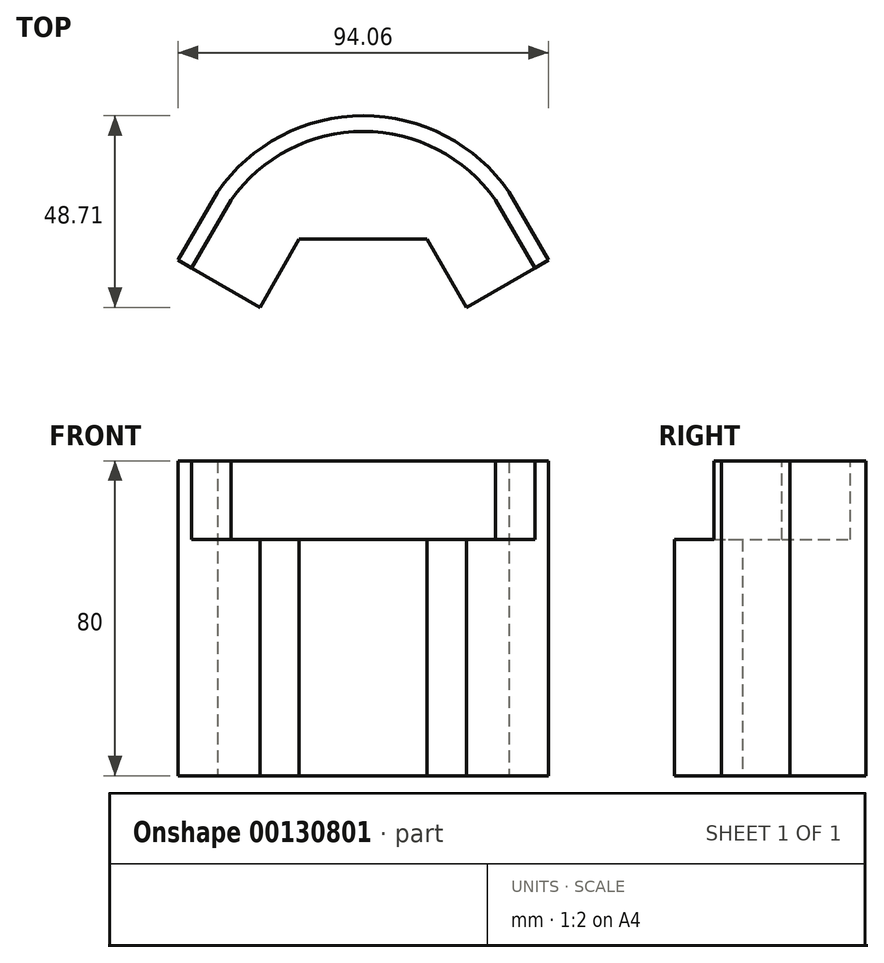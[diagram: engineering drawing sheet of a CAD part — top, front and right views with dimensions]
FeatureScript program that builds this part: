
annotation { "Feature Type Name" : "Feature", "Feature Type Description" : "" }
export const myFeature = defineFeature(function(context is Context, id is Id, definition is map)
    precondition{}
    {
        {
            var Q0;
            Q0=qCreatedBy(makeId("Top.planeOp"),FACE);
            var sketch = newSketch(context, id + "F0", { "sketchPlane" : qUnion([Q0])});
            skLineSegment(sketch, "E0", {"start": v(0, 0) * mm, "end": v(-43.57, -75.47) * mm});
            skLineSegment(sketch, "E1", {"start": v(0, -40) * mm, "end": v(-26.25, -85.47) * mm});
            skLineSegment(sketch, "E2", {"start": v(0, -40) * mm, "end": v(26.25, -85.47) * mm});
            skLineSegment(sketch, "E3", {"start": v(0, 0) * mm, "end": v(43.57, -75.47) * mm});
            skLineSegment(sketch, "E4", {"start": v(26.25, -85.47) * mm, "end": v(43.57, -75.47) * mm});
            skLineSegment(sketch, "E5", {"start": v(-26.25, -85.47) * mm, "end": v(-43.57, -75.47) * mm});
            skLineSegment(sketch, "E6", {"start": v(-33.57, -58.15) * mm, "end": v(-16.25, -68.15) * mm});
            skLineSegment(sketch, "E7", {"start": v(33.57, -58.15) * mm, "end": v(16.25, -68.15) * mm});
            skCircle(sketch, "E8", {"center": v(0, -77.53) * mm, "radius": 38.76 * mm});
            skSolve(sketch);
        }
        {
            var Q0;
            Q0=qCreatedBy(makeId("Top.planeOp"),FACE);
            var sketch = newSketch(context, id + "F1", { "sketchPlane" : qUnion([Q0])});
            skLineSegment(sketch, "E9", {"start": v(-26.25, -85.47) * mm, "end": v(-47.03, -73.47) * mm});
            skLineSegment(sketch, "E10", {"start": v(-47.03, -73.47) * mm, "end": v(-37.03, -56.15) * mm});
            skLineSegment(sketch, "E11", {"start": v(-26.25, -85.47) * mm, "end": v(-16.25, -68.15) * mm});
            skLineSegment(sketch, "E12", {"start": v(-16.25, -68.15) * mm, "end": v(16.25, -68.15) * mm});
            skLineSegment(sketch, "E13", {"start": v(16.25, -68.15) * mm, "end": v(26.25, -85.47) * mm});
            skLineSegment(sketch, "E14", {"start": v(26.25, -85.47) * mm, "end": v(47.03, -73.47) * mm});
            skLineSegment(sketch, "E15", {"start": v(47.03, -73.47) * mm, "end": v(37.03, -56.15) * mm});
            skArc(sketch, "E16", {"start": v(37.03, -56.15) * mm, "mid": v(0, -36.76) * mm, "end": v(-37.03, -56.15) * mm});
            skLineSegment(sketch, "E17", {"start": v(-16.25, -68.15) * mm, "end": v(-37.03, -56.15) * mm});
            skLineSegment(sketch, "E18", {"start": v(16.25, -68.15) * mm, "end": v(37.03, -56.15) * mm});
            skSolve(sketch);
        }
        {
            var Q0;
            Q0 = qSketchRegion(id + "F1", true);
            extrude(context, id + "F2", {"entities" : qUnion([Q0]), "depth" : 80 * mm});
        }
        {
            var Q0;
            Q0=makeQuery(id+"F2.opExtrude","CAP_FACE",FACE,{"disambiguationData":[OSD([sQuery(id+"F1.wireOp",EDGE,"E9"),sQuery(id+"F1.wireOp",EDGE,"E10"),sQuery(id+"F1.wireOp",EDGE,"E11"),sQuery(id+"F1.wireOp",EDGE,"E12"),sQuery(id+"F1.wireOp",EDGE,"E13"),sQuery(id+"F1.wireOp",EDGE,"E14"),sQuery(id+"F1.wireOp",EDGE,"E15"),sQuery(id+"F1.wireOp",EDGE,"E16")])],"isStart":false});
            var sketch = newSketch(context, id + "F3", { "sketchPlane" : qUnion([Q0])});
            skLineSegment(sketch, "E19", {"start": v(-26.25, -85.47) * mm, "end": v(-43.57, -75.47) * mm});
            skLineSegment(sketch, "E20", {"start": v(-43.57, -75.47) * mm, "end": v(-33.57, -58.15) * mm});
            skLineSegment(sketch, "E21", {"start": v(-26.25, -85.47) * mm, "end": v(-16.25, -68.15) * mm});
            skLineSegment(sketch, "E22", {"start": v(-16.25, -68.15) * mm, "end": v(16.25, -68.15) * mm});
            skLineSegment(sketch, "E23", {"start": v(16.25, -68.15) * mm, "end": v(26.25, -85.47) * mm});
            skLineSegment(sketch, "E24", {"start": v(26.25, -85.47) * mm, "end": v(43.57, -75.47) * mm});
            skLineSegment(sketch, "E25", {"start": v(43.57, -75.47) * mm, "end": v(33.57, -58.15) * mm});
            skArc(sketch, "E26", {"start": v(33.57, -58.15) * mm, "mid": v(0, -40.75) * mm, "end": v(-33.57, -58.15) * mm});
            skSolve(sketch);
        }
        {
            var Q0;
            Q0=makeQuery(id+"F3.imprint","IMPRINT",FACE,{"disambiguationData":[TD([[makeQuery(id+"F3.imprint","IMPRINT",EDGE,{"derivedFrom":sQuery(id+"F3.wireOp",EDGE,"E19")}),-1.0]])]});
            extrude(context, id + "F4", {"entities" : qUnion([Q0]), "operationType" : NewBodyOperationType.REMOVE, "oppositeDirection" : true, "depth" : 20 * mm});
        }
    });
